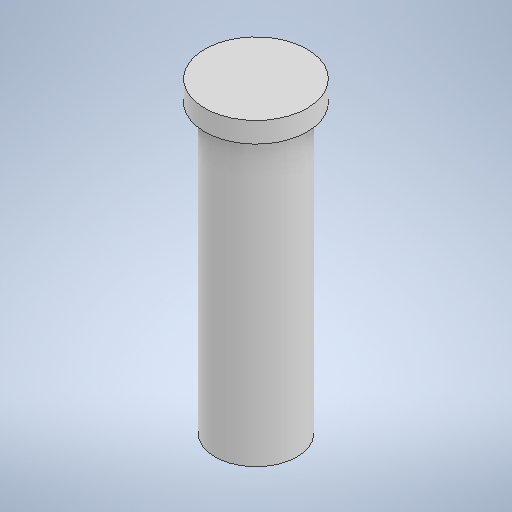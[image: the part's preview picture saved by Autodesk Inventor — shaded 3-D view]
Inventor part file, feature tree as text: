
AUTODESK INVENTOR PART (.ipt)
format: ipt  version: 2025.2 (Build 292293000, 293)  size: 224,256 bytes
history: native  units: mm
features: revolve x1, sketch x1
ambient origin geometry x8: Origin, YZ Plane, XZ Plane, XY Plane, X Axis, Y Axis, Z Axis, Center Point
bodies: Solid1 (feature_tree)
feature tree (2):
  revolve  "Revolution1"  [1 undecoded]
  sketch  "Sketch1"  dims[d0=30.0mm d1=5.0mm d2=2.0mm d3=1.0mm d4=28.0mm d5=4.0mm d6=90.0deg]
note: 1 required parameter value undecoded (feature->parameter linkage not recoverable at this tier; creation-order binding heuristic only, values carry confidence <= 0.55)
